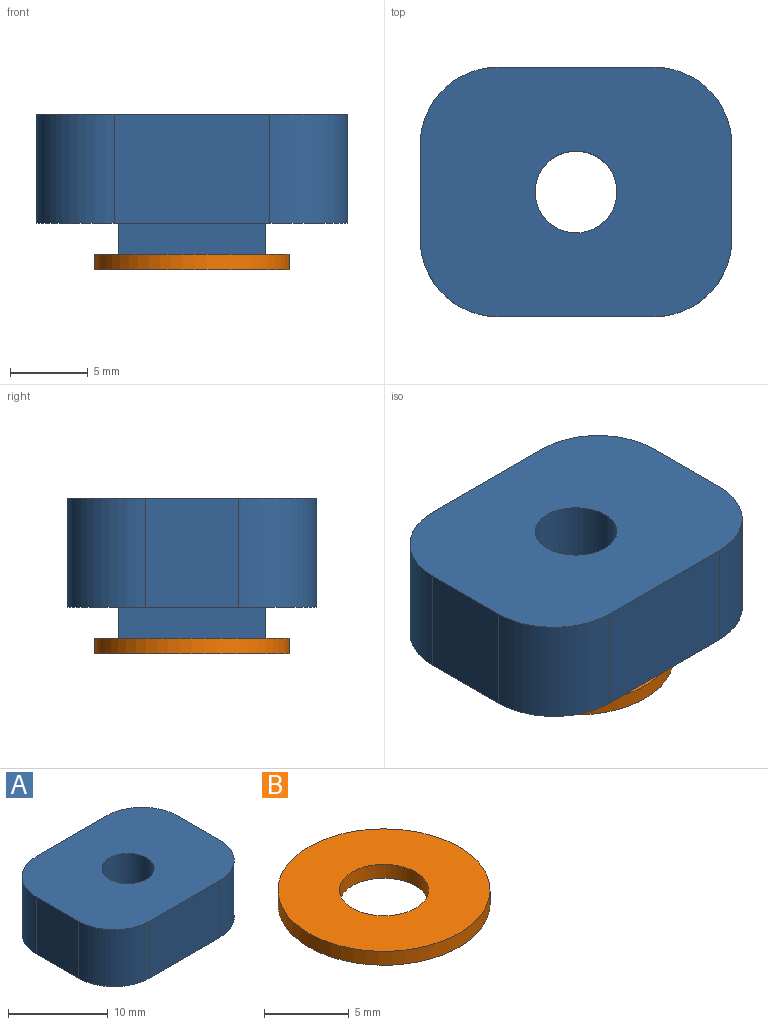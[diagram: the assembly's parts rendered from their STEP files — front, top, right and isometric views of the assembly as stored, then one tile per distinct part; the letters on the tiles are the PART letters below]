
ASSEMBLY  parts=2 mates=1
PART A: 16 faces, bbox 20x16x9 mm
  f0: plane 20x16mm, normal (0,0,-1), area 209.2mm2, adj f1,f2,f3,f4,f5,f6,f7,f8
  f1: plane 7x6mm, normal (-1,0,0), area 42mm2, adj f0,f2,f8,f10
  f2: cylinder r=5mm len=7mm, axis (0,0,-1), area 55mm2, adj f0,f1,f3,f10
  f3: plane 10x7mm, normal (0,-1,0), area 70mm2, adj f0,f2,f4,f10
  f4: cylinder r=5mm len=7mm, axis (0,0,-1), area 55mm2, adj f0,f3,f5,f10
  f5: plane 7x6mm, normal (1,0,0), area 42mm2, adj f0,f4,f6,f10
  f6: cylinder r=5mm len=7mm, axis (0,0,-1), area 55mm2, adj f0,f5,f7,f10
  f7: plane 10x7mm, normal (0,1,0), area 70mm2, adj f0,f6,f8,f10
  f8: cylinder r=5mm len=7mm, axis (0,0,-1), area 55mm2, adj f0,f1,f7,f10
  f9: cylinder r=2.62mm len=9mm, axis (0,0,-1), area 148.4mm2, adj f10,f15
  f10: plane 20x16mm, normal (0,0,1), area 276.9mm2, adj f1,f2,f3,f4,f5,f6,f7,f8
  f11: plane 9.45x2mm, normal (0,-1,0), area 18.9mm2, adj f0,f12,f14,f15
  f12: plane 9.45x2mm, normal (1,0,0), area 18.9mm2, adj f0,f11,f13,f15
  f13: plane 9.45x2mm, normal (0,1,0), area 18.9mm2, adj f0,f12,f14,f15
  f14: plane 9.45x2mm, normal (-1,0,0), area 18.9mm2, adj f0,f11,f13,f15
  f15: plane 9.45x9.45mm, normal (0,0,-1), area 67.7mm2, adj f9,f11,f12,f13,f14
PART B: 4 faces, bbox 12.5x12.5x1 mm
  f0: cylinder r=6.25mm len=12.5mm, axis (0,0,1), area 39.3mm2, adj f2,f3
  f1: cylinder r=2.62mm len=5.25mm, axis (0,0,1), area 16.5mm2, adj f2,f3
  f2: plane 12.5x12.5mm, normal (0,0,-1), area 101.1mm2, adj f0,f1
  f3: plane 12.5x12.5mm, normal (0,0,1), area 101.1mm2, adj f0,f1
PLACE A t=(3.99,-1.83,-3.7)mm
PLACE B t=(3.99,-1.83,-3.7)mm
MATE fastened A.f9 <-> B.f1  axis (0,0,-1) through (3.99,-1.83,-5.7)mm
